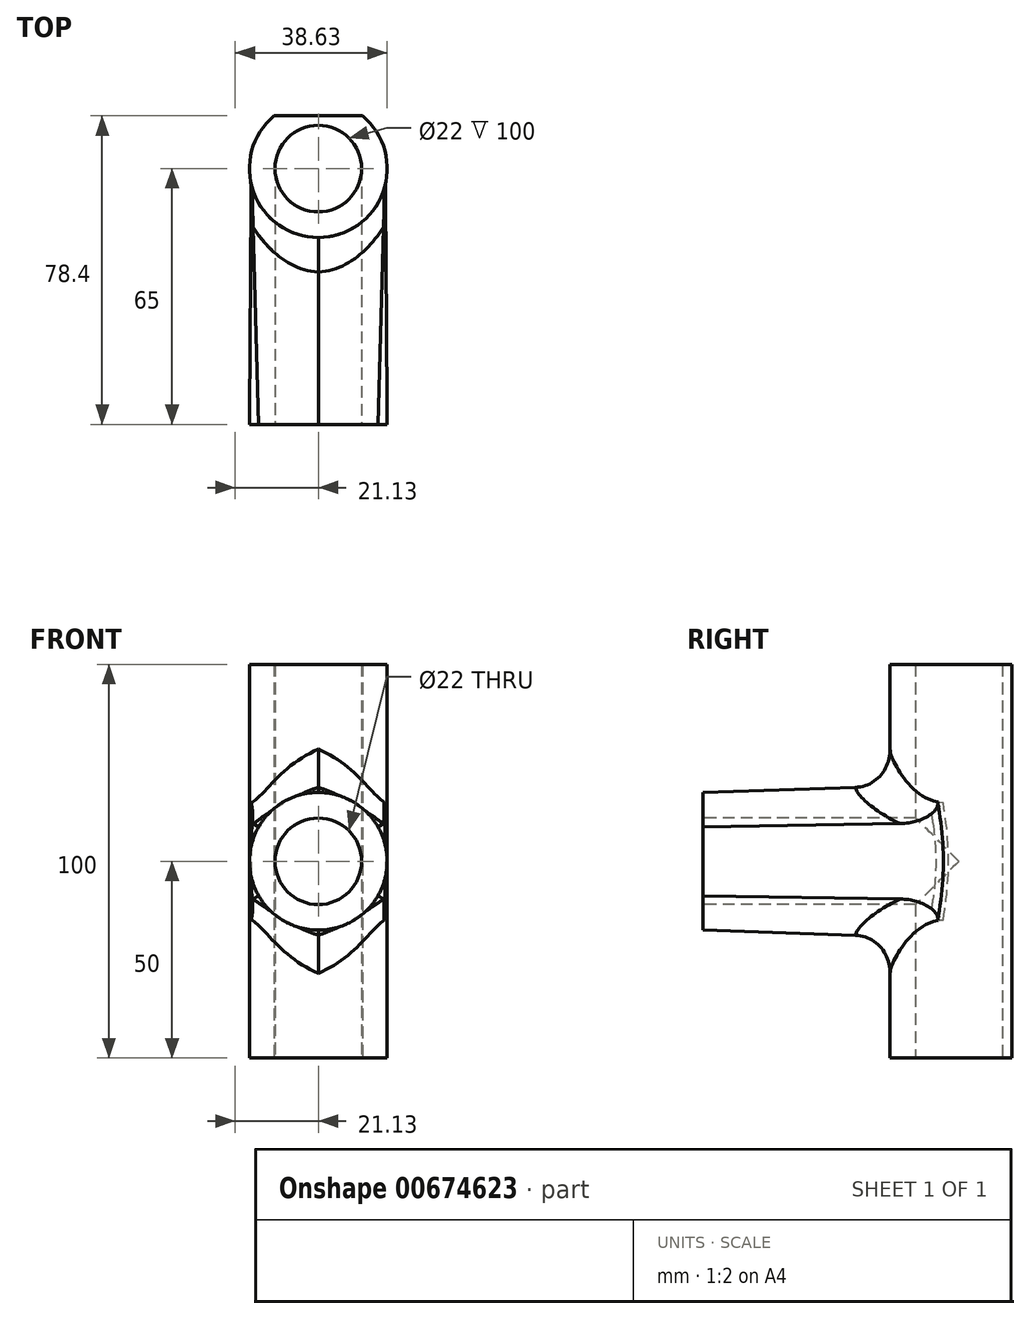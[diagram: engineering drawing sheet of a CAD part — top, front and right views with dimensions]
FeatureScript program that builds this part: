
annotation { "Feature Type Name" : "Feature", "Feature Type Description" : "" }
export const myFeature = defineFeature(function(context is Context, id is Id, definition is map)
    precondition{}
    {
        {
            var Q0;
            Q0=qCreatedBy(makeId("Top.planeOp"),FACE);
            var sketch = newSketch(context, id + "F0", { "sketchPlane" : qUnion([Q0])});
            skCircle(sketch, "E0", {"center": v(0, 0) * mm, "radius": 11 * mm});
            skLineSegment(sketch, "E1.bottom", {"start": v(20.39, 13.4) * mm, "end": v(-20.39, 13.4) * mm});
            skLineSegment(sketch, "E1.top", {"start": v(20.39, -13.4) * mm, "end": v(-20.39, -13.4) * mm});
            skLineSegment(sketch, "E1.left", {"start": v(20.39, 13.4) * mm, "end": v(20.39, -13.4) * mm});
            skLineSegment(sketch, "E1.right", {"start": v(-20.39, 13.4) * mm, "end": v(-20.39, -13.4) * mm});
            skCircle(sketch, "E2", {"center": v(0, 0) * mm, "radius": 17.5 * mm});
            skSolve(sketch);
        }
        {
            var Q0;
            Q0=qCreatedBy(makeId("Front.planeOp"),FACE);
            cPlane(context, id + "F1", {"entities" : qUnion([Q0]), "cplaneType" : CPlaneType.OFFSET, "offset" : 65 * mm, "width" : 150 * mm, "height" : 150 * mm});
        }
        {
            var Q0;
            Q0=makeQuery(id+"F0.imprint","IMPRINT",FACE,{"disambiguationData":[TD([[makeQuery(id+"F0.imprint","IMPRINT",EDGE,{"derivedFrom":sQuery(id+"F0.wireOp",EDGE,"E0")}),-1.0]])]});
            var Q1;
            {var subQ0=sQuery(id+"F0.wireOp",EDGE,"E2");var subQ1=sQuery(id+"F0.wireOp",EDGE,"E1.top");var subQ2=makeQuery(id+"F0.imprint","INTERSECT",VERTEX,{"disambiguationData":[OD(0.0)],"derivedFrom":[subQ1,subQ0]});Q1=makeQuery(id+"F0.imprint","IMPRINT",FACE,{"disambiguationData":[TD([[makeQuery(id+"F0.imprint","IMPRINT",EDGE,{"disambiguationData":[TD([[subQ2,-1.0]])],"derivedFrom":subQ1}),1.0]])]});}
            extrude(context, id + "F2", {"entities" : qUnion([Q0, Q1]), "endBound" : BoundingType.SYMMETRIC, "depth" : 100 * mm, "offsetDistance" : 25 * mm});
        }
        {
            var Q0;
            Q0=qCreatedBy(id+"F1.planeOp",FACE);
            var sketch = newSketch(context, id + "F3", { "sketchPlane" : qUnion([Q0])});
            skCircle(sketch, "E3", {"center": v(0, 0) * mm, "radius": 17.5 * mm});
            skSolve(sketch);
        }
        {
            var Q0;
            Q0=qCreatedBy(makeId("Front.planeOp"),FACE);
            var sketch = newSketch(context, id + "F4", { "sketchPlane" : qUnion([Q0])});
            skCircle(sketch, "E4.cCircle", {"center": v(0, 0) * mm, "radius": 17.01 * mm, "construction": true});
            skLineSegment(sketch, "E4.0", {"start": v(17.01, 9.82) * mm, "end": v(17.01, -9.82) * mm});
            skLineSegment(sketch, "E4.1", {"start": v(17.01, -9.82) * mm, "end": v(0, -19.65) * mm});
            skLineSegment(sketch, "E4.2", {"start": v(0, -19.65) * mm, "end": v(-17.01, -9.82) * mm});
            skLineSegment(sketch, "E4.3", {"start": v(-17.01, -9.82) * mm, "end": v(-17.01, 9.82) * mm});
            skLineSegment(sketch, "E4.4", {"start": v(-17.01, 9.82) * mm, "end": v(0, 19.65) * mm});
            skLineSegment(sketch, "E4.5", {"start": v(0, 19.65) * mm, "end": v(17.01, 9.82) * mm});
            skPoint(sketch, "E4.0.midPoint", {"position": v(17.01, 0) * mm});
            skSolve(sketch);
        }
        {
            var Q1;
            Q1=makeQuery(id+"F4.imprint","IMPRINT",FACE,{"disambiguationData":[TD([[makeQuery(id+"F4.imprint","IMPRINT",EDGE,{"derivedFrom":sQuery(id+"F4.wireOp",EDGE,"E4.0")}),-1.0]])]});
            var Q2;
            Q2=makeQuery(id+"F3.imprint","IMPRINT",FACE,{"disambiguationData":[TD([[makeQuery(id+"F3.imprint","IMPRINT",EDGE,{"derivedFrom":sQuery(id+"F3.wireOp",EDGE,"E3")}),1.0]])]});
            loft(context, id + "F5", {"operationType" : NewBodyOperationType.ADD, "sheetProfilesArray" : [{ "sheetProfileEntities" : qUnion([Q1]) }, { "sheetProfileEntities" : qUnion([Q2]) }]});
        }
        {
            var Q0;
            Q0=makeQuery(id+"F5.opLoft","CAP_FACE",FACE,{"disambiguationData":[OSD([makeQuery(id+"F3.imprint","IMPRINT",FACE,{"disambiguationData":[TD([[makeQuery(id+"F3.imprint","IMPRINT",EDGE,{"derivedFrom":sQuery(id+"F3.wireOp",EDGE,"E3")}),1.0]])]})])],"isStart":true});
            var sketch = newSketch(context, id + "F6", { "sketchPlane" : qUnion([Q0])});
            skCircle(sketch, "E5", {"center": v(0, 0) * mm, "radius": 11 * mm});
            skSolve(sketch);
        }
        {
            var Q0;
            Q0=makeQuery(id+"F6.imprint","IMPRINT",FACE,{"disambiguationData":[TD([[makeQuery(id+"F6.imprint","IMPRINT",EDGE,{"derivedFrom":sQuery(id+"F6.wireOp",EDGE,"E5")}),1.0]])]});
            var Q1;
            Q1=sQuery(id+"F6.wireOp",EDGE,"E5");
            extrude(context, id + "F7", {"entities" : qUnion([Q0]), "operationType" : NewBodyOperationType.REMOVE, "surfaceEntities" : qUnion([Q1]), "oppositeDirection" : true, "depth" : 65 * mm, "offsetDistance" : 25 * mm});
        }
        {
            var Q0;
            Q0=makeQuery(id+"F0.imprint","IMPRINT",FACE,{"disambiguationData":[TD([[makeQuery(id+"F0.imprint","IMPRINT",EDGE,{"derivedFrom":sQuery(id+"F0.wireOp",EDGE,"E0")}),1.0]])]});
            var Q1;
            Q1=sQuery(id+"F0.wireOp",EDGE,"E0");
            extrude(context, id + "F8", {"entities" : qUnion([Q0]), "operationType" : NewBodyOperationType.REMOVE, "surfaceEntities" : qUnion([Q1]), "endBound" : BoundingType.SYMMETRIC, "oppositeDirection" : true, "depth" : 100 * mm, "offsetDistance" : 25 * mm});
        }
        {
            var Q0;
            Q0=makeQuery(id+"F5.boolean.opBoolean","INTERSECT",EDGE,{"derivedFrom":[makeQuery(id+"F2.opExtrude","SWEPT_FACE",FACE,{"disambiguationData":[OSD([sQuery(id+"F0.wireOp",EDGE,"E2")])]}),makeQuery(id+"F5.opLoft","SWEPT_FACE",FACE,{"disambiguationData":[OSD([sQuery(id+"F3.wireOp",EDGE,"E3"),sQuery(id+"F4.wireOp",EDGE,"E4.0"),sQuery(id+"F4.wireOp",EDGE,"E4.3"),sQuery(id+"F4.wireOp",EDGE,"E4.4"),sQuery(id+"F4.wireOp",EDGE,"E4.5")])]})]});
            var Q1;
            Q1=makeQuery(id+"F5.boolean.opBoolean","INTERSECT",EDGE,{"derivedFrom":[makeQuery(id+"F2.opExtrude","SWEPT_FACE",FACE,{"disambiguationData":[OSD([sQuery(id+"F0.wireOp",EDGE,"E2")])]}),makeQuery(id+"F5.opLoft","SWEPT_FACE",FACE,{"disambiguationData":[OSD([sQuery(id+"F3.wireOp",EDGE,"E3"),sQuery(id+"F4.wireOp",EDGE,"E4.1"),sQuery(id+"F4.wireOp",EDGE,"E4.2"),sQuery(id+"F4.wireOp",EDGE,"E4.3"),sQuery(id+"F4.wireOp",EDGE,"E4.4")])]})]});
            var Q2;
            Q2=makeQuery(id+"F5.boolean.opBoolean","INTERSECT",EDGE,{"derivedFrom":[makeQuery(id+"F2.opExtrude","SWEPT_FACE",FACE,{"disambiguationData":[OSD([sQuery(id+"F0.wireOp",EDGE,"E2")])]}),makeQuery(id+"F5.opLoft","SWEPT_FACE",FACE,{"disambiguationData":[OSD([sQuery(id+"F3.wireOp",EDGE,"E3"),sQuery(id+"F4.wireOp",EDGE,"E4.0"),sQuery(id+"F4.wireOp",EDGE,"E4.4"),sQuery(id+"F4.wireOp",EDGE,"E4.5")])]})]});
            var Q3;
            Q3=makeQuery(id+"F5.boolean.opBoolean","INTERSECT",EDGE,{"derivedFrom":[makeQuery(id+"F2.opExtrude","SWEPT_FACE",FACE,{"disambiguationData":[OSD([sQuery(id+"F0.wireOp",EDGE,"E2")])]}),makeQuery(id+"F5.opLoft","SWEPT_FACE",FACE,{"disambiguationData":[OSD([sQuery(id+"F3.wireOp",EDGE,"E3"),sQuery(id+"F4.wireOp",EDGE,"E4.0"),sQuery(id+"F4.wireOp",EDGE,"E4.1"),sQuery(id+"F4.wireOp",EDGE,"E4.2"),sQuery(id+"F4.wireOp",EDGE,"E4.3")])]})]});
            fillet(context, id + "F9", {"entities" : qUnion([Q0, Q1, Q2, Q3]), "radius" : 9.25 * mm, "tangentPropagation" : true, "allowEdgeOverflow" : false});
        }
        {
            var Q0;
            Q0=makeQuery(id+"F5.boolean.opBoolean","INTERSECT",EDGE,{"derivedFrom":[makeQuery(id+"F2.opExtrude","SWEPT_FACE",FACE,{"disambiguationData":[OSD([sQuery(id+"F0.wireOp",EDGE,"E2")])]}),makeQuery(id+"F5.opLoft","SWEPT_FACE",FACE,{"disambiguationData":[OSD([sQuery(id+"F3.wireOp",EDGE,"E3"),sQuery(id+"F4.wireOp",EDGE,"E4.2"),sQuery(id+"F4.wireOp",EDGE,"E4.3"),sQuery(id+"F4.wireOp",EDGE,"E4.4"),sQuery(id+"F4.wireOp",EDGE,"E4.5")])]})]});
            var Q1;
            Q1=makeQuery(id+"F5.boolean.opBoolean","INTERSECT",EDGE,{"derivedFrom":[makeQuery(id+"F2.opExtrude","SWEPT_FACE",FACE,{"disambiguationData":[OSD([sQuery(id+"F0.wireOp",EDGE,"E2")])]}),makeQuery(id+"F5.opLoft","SWEPT_FACE",FACE,{"disambiguationData":[OSD([sQuery(id+"F3.wireOp",EDGE,"E3"),sQuery(id+"F4.wireOp",EDGE,"E4.0"),sQuery(id+"F4.wireOp",EDGE,"E4.1"),sQuery(id+"F4.wireOp",EDGE,"E4.2"),sQuery(id+"F4.wireOp",EDGE,"E4.5")])]})]});
            fillet(context, id + "F10", {"entities" : qUnion([Q0, Q1]), "radius" : 20 * mm, "tangentPropagation" : true, "allowEdgeOverflow" : false});
        }
    });
